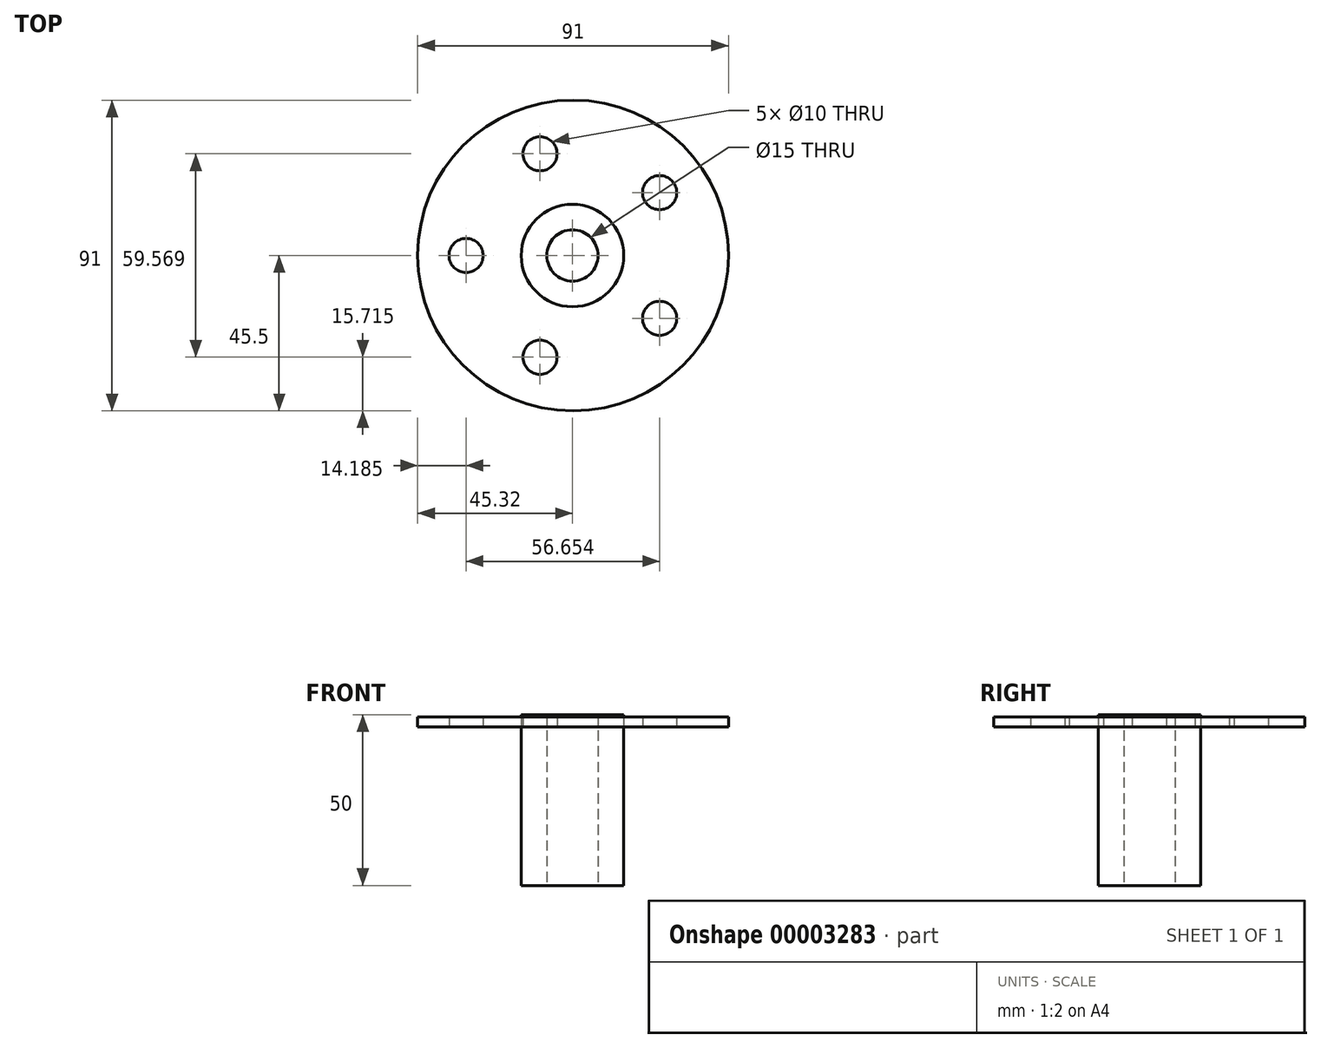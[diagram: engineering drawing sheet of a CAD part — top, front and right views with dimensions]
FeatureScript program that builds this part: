
annotation { "Feature Type Name" : "Feature", "Feature Type Description" : "" }
export const myFeature = defineFeature(function(context is Context, id is Id, definition is map)
    precondition{}
    {
        {
            var Q0;
            Q0=qCreatedBy(makeId("Top.planeOp"),FACE);
            var sketch = newSketch(context, id + "F0", { "sketchPlane" : qUnion([Q0])});
            skCircle(sketch, "E0", {"center": v(0, 0) * mm, "radius": 15 * mm});
            skCircle(sketch, "E1", {"center": v(0, 0) * mm, "radius": 7.5 * mm});
            skSolve(sketch);
        }
        {
            var Q0;
            Q0=makeQuery(id+"F0.imprint","IMPRINT",FACE,{"disambiguationData":[TD([[makeQuery(id+"F0.imprint","IMPRINT",EDGE,{"derivedFrom":sQuery(id+"F0.wireOp",EDGE,"E0")}),1.0]])]});
            extrude(context, id + "F1", {"entities" : qUnion([Q0]), "depth" : 50 * mm, "symmetric" : true});
        }
        {
            var Q0;
            Q0=makeQuery(id+"F1.opExtrude","CAP_FACE",FACE,{"disambiguationData":[OSD([sQuery(id+"F0.wireOp",EDGE,"E0"),sQuery(id+"F0.wireOp",EDGE,"E1")])],"isStart":false});
            var sketch = newSketch(context, id + "F2", { "sketchPlane" : qUnion([Q0])});
            skCircle(sketch, "E2", {"center": v(0.18, 0) * mm, "radius": 15.5 * mm});
            skCircle(sketch, "E3.0", {"center": v(0.18, 0) * mm, "radius": 45.5 * mm});
            skCircle(sketch, "E4", {"center": v(-31.14, 0) * mm, "radius": 5 * mm});
            skSolve(sketch);
        }
        {
            var Q0;
            {var subQ0=makeQuery(id+"F2.imprint","IMPRINT",EDGE,{"derivedFrom":makeQuery(id+"F1.opExtrude","CAP_EDGE",EDGE,{"disambiguationData":[OSD([sQuery(id+"F0.wireOp",EDGE,"E1")])],"isStart":false})});var subQ1=makeQuery(id+"F2.imprint","IMPRINT",EDGE,{"derivedFrom":sQuery(id+"F2.wireOp",EDGE,"E2")});var subQ2=makeQuery(id+"F2.imprint","IMPRINT",EDGE,{"derivedFrom":makeQuery(id+"F1.opExtrude","CAP_EDGE",EDGE,{"disambiguationData":[OSD([sQuery(id+"F0.wireOp",EDGE,"E0")])],"isStart":false})});Q0=qUnion([makeQuery(id+"F2.imprint","IMPRINT",FACE,{"disambiguationData":[TD([[subQ0,1.0]])]}),makeQuery(id+"F2.imprint","IMPRINT",FACE,{"disambiguationData":[TD([[subQ1,-1.0]])]}),makeQuery(id+"F2.imprint","IMPRINT",FACE,{"disambiguationData":[TD([[subQ1,1.0]])]}),makeQuery(id+"F2.imprint","IMPRINT",FACE,{"disambiguationData":[TD([[subQ2,1.0]])]})]);}
            extrude(context, id + "F3", {"entities" : qUnion([Q0]), "depth" : 3 * mm});
        }
        {
            var Q0;
            Q0=makeQuery(id+"F3.opExtrude","SWEPT_FACE",FACE,{"disambiguationData":[OSD([sQuery(id+"F2.wireOp",EDGE,"E4")])]});
            var Q1;
            Q1=makeQuery(id+"F3.opExtrude","CAP_EDGE",EDGE,{"disambiguationData":[OSD([sQuery(id+"F2.wireOp",EDGE,"E3.0")])],"isStart":false});
            circularPattern(context, id + "F4", {"faces" : qUnion([Q0]), "axis" : qUnion([Q1]), "angle" : 360 * degree, "instanceCount" : 5, "equalSpace" : true, "patternType" : PatternType.FACE});
        }
        {
            var Q0;
            Q0=makeQuery(id+"F3.opExtrude","SWEPT_BODY",BODY,{"disambiguationData":[OSD([sQuery(id+"F2.wireOp",EDGE,"E3.0"),sQuery(id+"F2.wireOp",EDGE,"E4")])]});
            transform(context, id + "F5", {"entities" : qUnion([Q0]), "transformType" : TransformType.TRANSLATION_3D, "dx" : 0 * mm, "dy" : 0 * mm, "dz" : -3.59 * mm, "makeCopy" : false});
        }
    });
